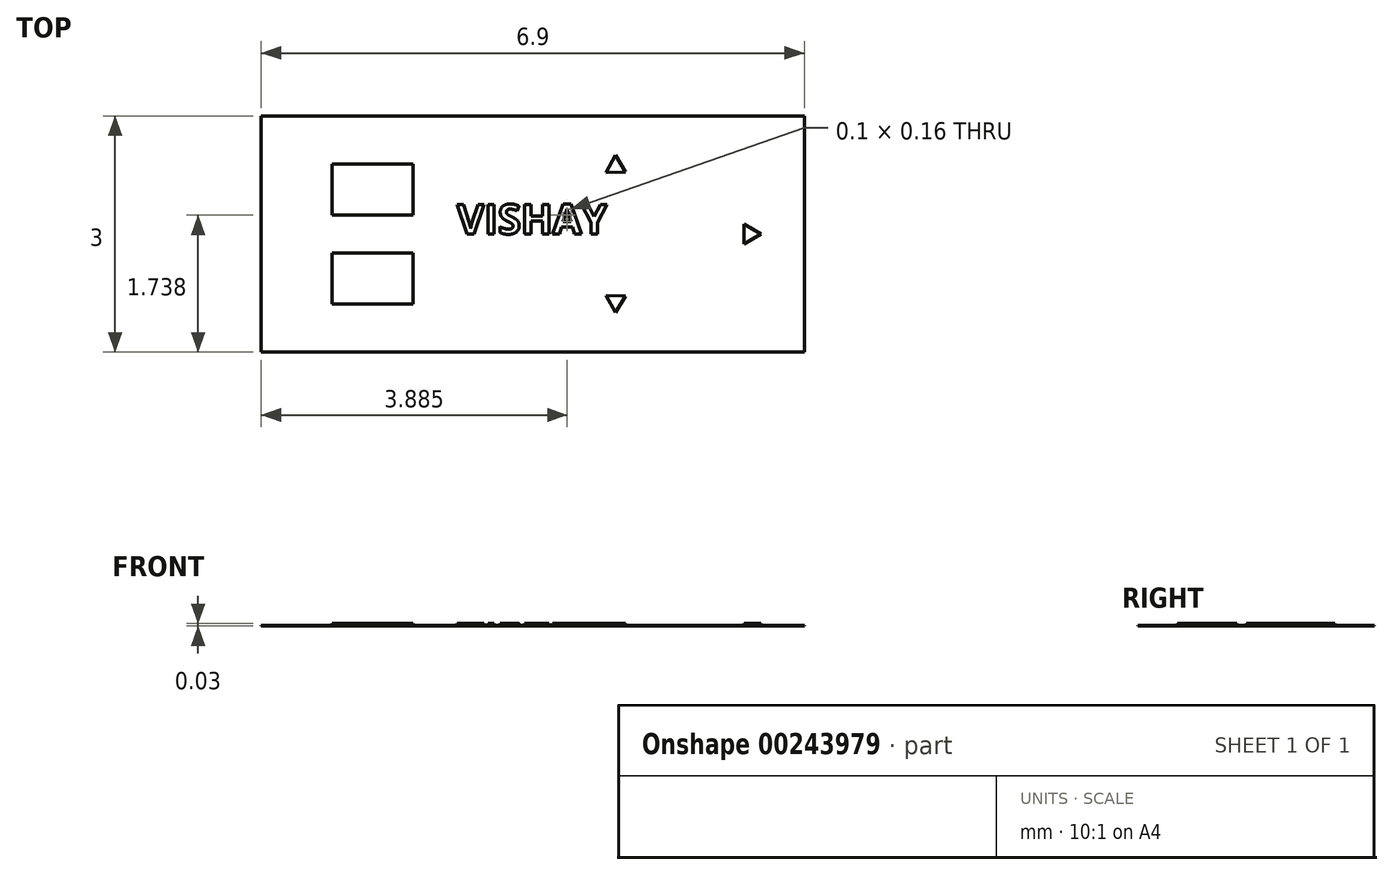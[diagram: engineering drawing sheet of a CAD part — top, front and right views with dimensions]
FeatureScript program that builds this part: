
annotation { "Feature Type Name" : "Feature", "Feature Type Description" : "" }
export const myFeature = defineFeature(function(context is Context, id is Id, definition is map)
    precondition{}
    {
        {
            var Q0;
            Q0=qCreatedBy(makeId("Top.planeOp"),FACE);
            var sketch = newSketch(context, id + "F0", { "sketchPlane" : qUnion([Q0])});
            skLineSegment(sketch, "E0.rect.bottom", {"start": v(3.45, -1.5) * mm, "end": v(-3.45, -1.5) * mm});
            skLineSegment(sketch, "E0.rect.top", {"start": v(3.45, 1.5) * mm, "end": v(-3.45, 1.5) * mm});
            skLineSegment(sketch, "E0.rect.left", {"start": v(3.45, -1.5) * mm, "end": v(3.45, 1.5) * mm});
            skLineSegment(sketch, "E0.rect.right", {"start": v(-3.45, -1.5) * mm, "end": v(-3.45, 1.5) * mm});
            skPoint(sketch, "E0.rect.middle", {"position": v(0, 0) * mm});
            skSolve(sketch);
        }
        {
            var Q0;
            Q0=qSketchRegion(id+"F0",true);
            extrude(context, id + "F1", {"entities" : qUnion([Q0]), "depth" : 0.01 * mm});
        }
        {
            var Q0;
            Q0=makeQuery(id+"F1.opExtrude","CAP_FACE",FACE,{"disambiguationData":[OSD([sQuery(id+"F0.wireOp",EDGE,"E0.rect.bottom"),sQuery(id+"F0.wireOp",EDGE,"E0.rect.top"),sQuery(id+"F0.wireOp",EDGE,"E0.rect.left"),sQuery(id+"F0.wireOp",EDGE,"E0.rect.right")])],"isStart":false});
            var sketch = newSketch(context, id + "F2", { "sketchPlane" : qUnion([Q0])});
            skLineSegment(sketch, "E1.rect.right", {"start": v(2.55, 0.89) * mm, "end": v(2.55, -0.89) * mm});
            skPoint(sketch, "E1.rect.middle", {"position": v(0, 0) * mm});
            skLineSegment(sketch, "E2", {"start": v(1.05, 1) * mm, "end": v(0.93, 0.78) * mm});
            skLineSegment(sketch, "E3", {"start": v(0.93, 0.78) * mm, "end": v(1.18, 0.79) * mm});
            skLineSegment(sketch, "E4", {"start": v(1.18, 0.79) * mm, "end": v(1.05, 1) * mm});
            skLineSegment(sketch, "E5", {"start": v(3.57, 0) * mm, "end": v(-3.45, 0) * mm, "construction": true});
            skPoint(sketch, "E5.startSnap0", {"position": v(3.45, 0) * mm});
            skLineSegment(sketch, "E6.MirrorCS", {"start": v(0.93, -0.78) * mm, "end": v(1.18, -0.79) * mm});
            skLineSegment(sketch, "E7.MirrorCS", {"start": v(1.18, -0.79) * mm, "end": v(1.05, -1) * mm});
            skLineSegment(sketch, "E8.MirrorCS", {"start": v(1.05, -1) * mm, "end": v(0.93, -0.78) * mm});
            skLineSegment(sketch, "E9.bottom", {"start": v(-2.55, 0.89) * mm, "end": v(-1.52, 0.89) * mm});
            skLineSegment(sketch, "E9.top", {"start": v(-2.55, 0.24) * mm, "end": v(-1.52, 0.24) * mm});
            skLineSegment(sketch, "E9.left", {"start": v(-2.55, 0.89) * mm, "end": v(-2.55, 0.24) * mm});
            skLineSegment(sketch, "E9.right", {"start": v(-1.52, 0.89) * mm, "end": v(-1.52, 0.24) * mm});
            skLineSegment(sketch, "E10.MirrorCS", {"start": v(-2.55, -0.24) * mm, "end": v(-1.52, -0.24) * mm});
            skLineSegment(sketch, "E11.MirrorCS", {"start": v(-1.52, -0.89) * mm, "end": v(-1.52, -0.24) * mm});
            skLineSegment(sketch, "E12.MirrorCS", {"start": v(-2.55, -0.9) * mm, "end": v(-1.52, -0.89) * mm});
            skLineSegment(sketch, "E13.MirrorCS", {"start": v(-2.55, -0.9) * mm, "end": v(-2.55, -0.24) * mm});
            skLineSegment(sketch, "E14", {"start": v(2.9, 0) * mm, "end": v(2.68, 0.12) * mm});
            skLineSegment(sketch, "E15", {"start": v(2.68, 0.12) * mm, "end": v(2.68, -0.13) * mm});
            skLineSegment(sketch, "E16", {"start": v(2.68, -0.12) * mm, "end": v(2.9, 0) * mm});
            skText(sketch, "E17", { "text": "VISHAY", "fontName": "OpenSans-Bold.ttf"});
            const initialGuessF2  = {"E17": [-0.00096, 0, 1, 0, 0.00038]};
            skSetInitialGuess(sketch, initialGuessF2);
            skSolve(sketch);
        }
        {
            var Q0;
            Q0=qSketchRegion(id+"F2",true);
            extrude(context, id + "F3", {"entities" : qUnion([Q0]), "depth" : 0.02 * mm});
        }
    });
